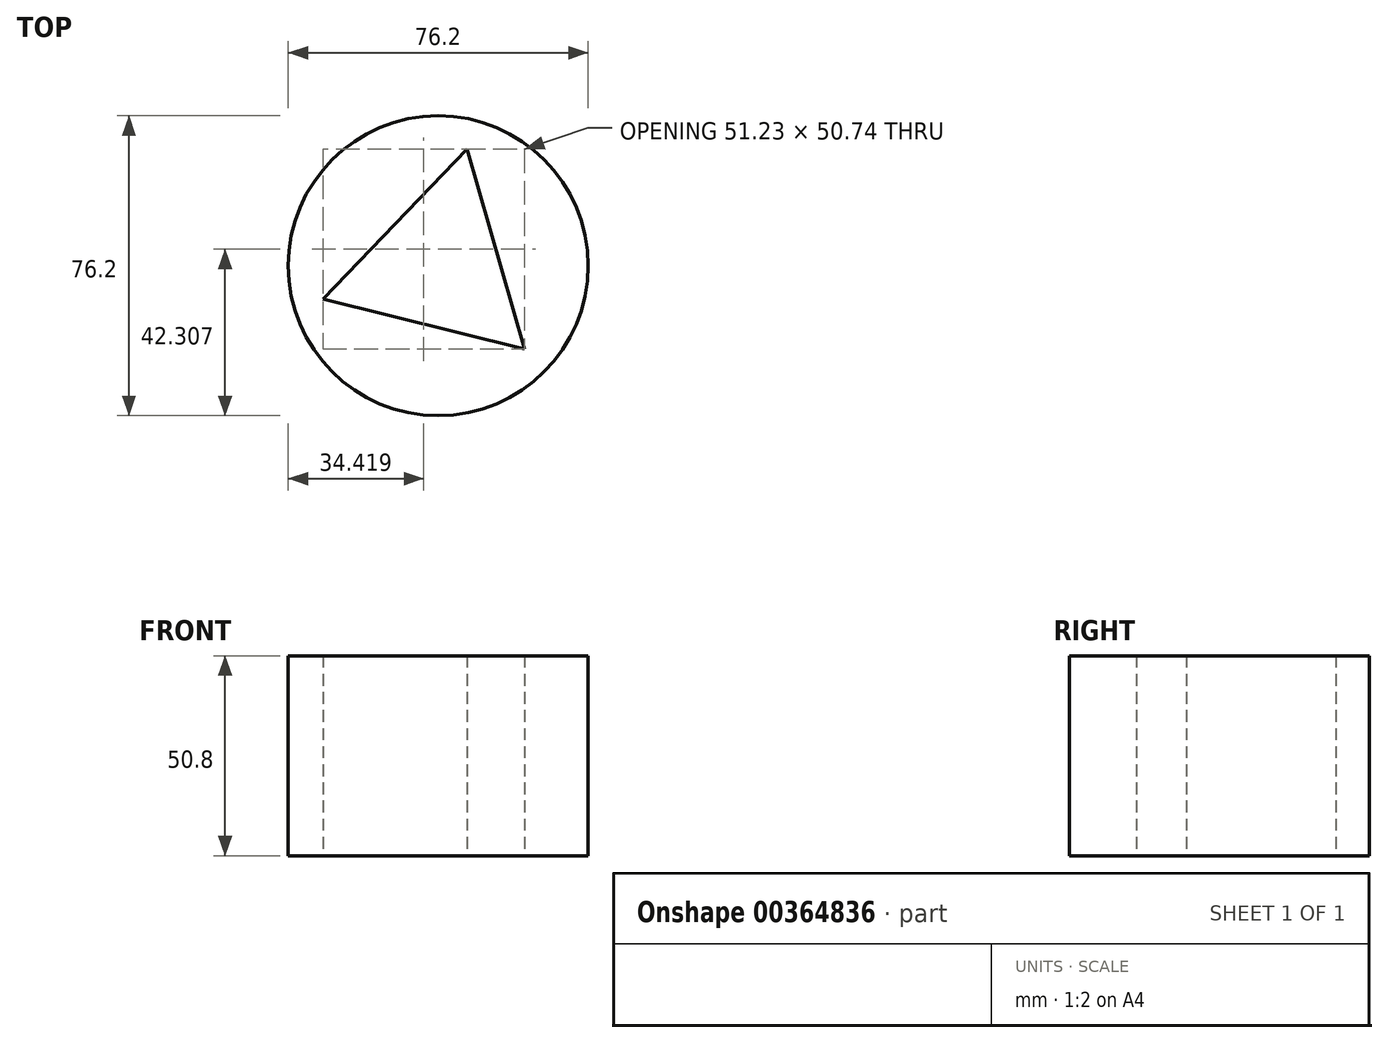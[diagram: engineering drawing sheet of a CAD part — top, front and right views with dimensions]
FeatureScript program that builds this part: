
annotation { "Feature Type Name" : "Feature", "Feature Type Description" : "" }
export const myFeature = defineFeature(function(context is Context, id is Id, definition is map)
    precondition{}
    {
        {
            var Q0;
            Q0=qCreatedBy(makeId("Top.planeOp"),FACE);
            var sketch = newSketch(context, id + "F0", { "sketchPlane" : qUnion([Q0])});
            skCircle(sketch, "E0", {"center": v(0, 0) * mm, "radius": 38.1 * mm});
            skSolve(sketch);
        }
        {
            var Q0;
            Q0=makeQuery(id+"F0.imprint","IMPRINT",FACE,{"disambiguationData":[TD([[makeQuery(id+"F0.imprint","IMPRINT",EDGE,{"derivedFrom":sQuery(id+"F0.wireOp",EDGE,"E0")}),1.0]])]});
            extrude(context, id + "F1", {"entities" : qUnion([Q0]), "depth" : 50.8 * mm});
        }
        {
            var Q0;
            Q0=qCreatedBy(makeId("Top.planeOp"),FACE);
            var sketch = newSketch(context, id + "F2", { "sketchPlane" : qUnion([Q0])});
            skCircle(sketch, "E1.cCircle", {"center": v(0, 0) * mm, "radius": 15.24 * mm, "construction": true});
            skLineSegment(sketch, "E1.0", {"start": v(-29.3, -8.41) * mm, "end": v(7.36, 29.58) * mm});
            skLineSegment(sketch, "E1.1", {"start": v(7.36, 29.58) * mm, "end": v(21.93, -21.16) * mm});
            skLineSegment(sketch, "E1.2", {"start": v(21.93, -21.16) * mm, "end": v(-29.3, -8.41) * mm});
            skPoint(sketch, "E1.0.midPoint", {"position": v(-10.97, 10.58) * mm});
            skSolve(sketch);
        }
        {
            var Q0;
            Q0 = qSketchRegion(id + "F2", true);
            extrude(context, id + "F3", {"entities" : qUnion([Q0]), "operationType" : NewBodyOperationType.REMOVE, "depth" : 50.8 * mm});
        }
    });
